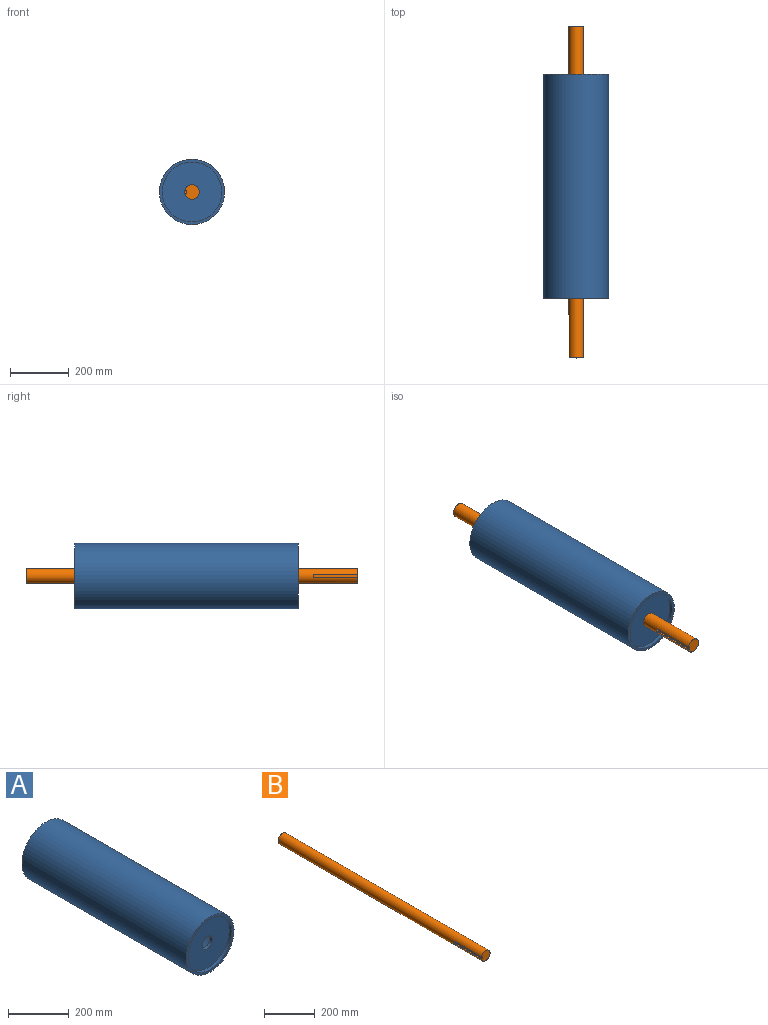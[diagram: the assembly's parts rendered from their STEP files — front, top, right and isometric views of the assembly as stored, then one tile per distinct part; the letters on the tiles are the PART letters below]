
ASSEMBLY  parts=2 mates=1
PART A: 12 faces, bbox 222.3x762x222.3 mm
  f0: cylinder r=101.6mm len=711.2mm, axis (0,1,0), area 454009.9mm2, adj f7,f10
  f1: cylinder r=101.6mm len=203.2mm, axis (0,1,0), area 8107.3mm2, adj f5,f11
  f2: cylinder r=101.6mm len=203.2mm, axis (0,1,0), area 8107.3mm2, adj f4,f8
  f3: cylinder r=111.12mm len=762mm, axis (0,1,0), area 532042.9mm2, adj f4,f5
  f4: plane 222.25x222.25mm, normal (0,-1,0), area 6365.5mm2, adj f2,f3
  f5: plane 222.25x222.25mm, normal (0,1,0), area 6365.5mm2, adj f1,f3
  f6: cylinder r=24.61mm len=49.21mm, axis (0,-1,0), area 1963.5mm2, adj f7,f8
  f7: plane 203.2x203.2mm, normal (0,1,0), area 30527.1mm2, adj f0,f6
  f8: plane 203.2x203.2mm, normal (0,-1,0), area 30527.1mm2, adj f2,f6
  f9: cylinder r=24.61mm len=49.21mm, axis (0,1,0), area 1963.5mm2, adj f10,f11
  f10: plane 203.2x203.2mm, normal (0,-1,0), area 30527.1mm2, adj f0,f9
  f11: plane 203.2x203.2mm, normal (0,1,0), area 30527.1mm2, adj f1,f9
PART B: 7 faces, bbox 49.2x1130.3x49.2 mm
  f0: cylinder r=24.61mm len=1130.3mm, axis (0,1,0), area 172810.8mm2, adj f1,f2,f4,f5,f6
  f1: plane 49.21x48.38mm, normal (0,-1,0), area 1825mm2, adj f0,f3,f4,f5
  f2: plane 49.21x49.21mm, normal (0,1,0), area 1902.1mm2, adj f0
  f3: plane 152.4x12.7mm, normal (-1,0,0), area 1918.2mm2, adj f1,f4,f5,f6
  f4: plane 146.05x5.52mm, normal (0,0,-1), area 805.7mm2, adj f0,f1,f3,f6
  f5: plane 146.05x5.52mm, normal (0,0,1), area 805.7mm2, adj f0,f1,f3,f6
  f6: cylinder r=6.35mm len=12.7mm, axis (1,0,0), area 118.4mm2, adj f0,f3,f4,f5
PLACE A at identity fixed
PLACE B t=(0,-19.05,0)mm
MATE fastened A.f0 <-> B.f0  axis (0,-1,0) through (0,-368.3,0)mm
